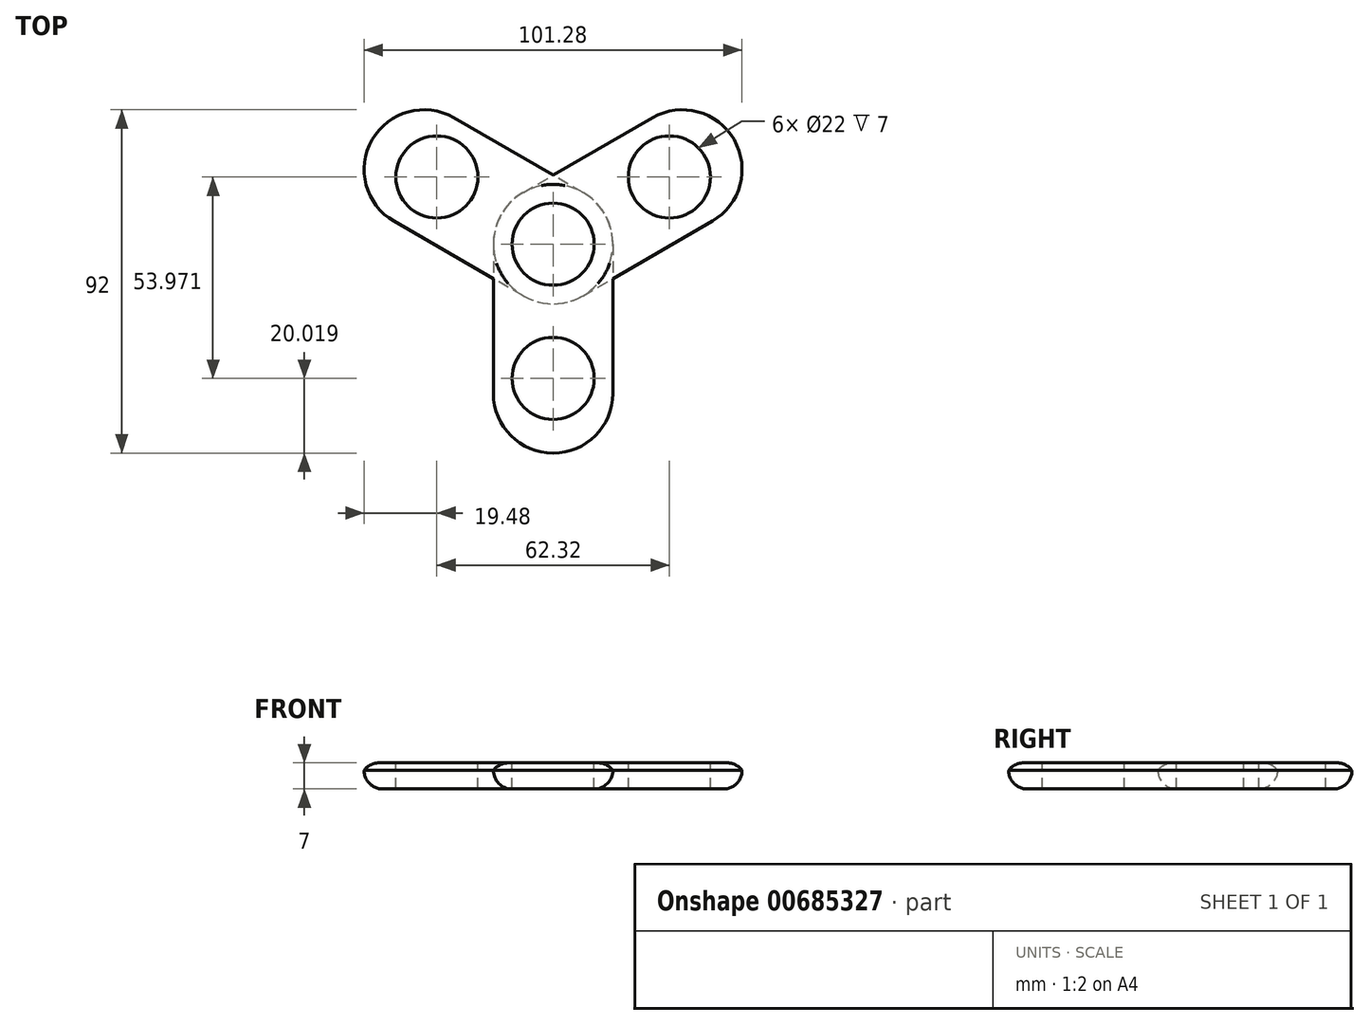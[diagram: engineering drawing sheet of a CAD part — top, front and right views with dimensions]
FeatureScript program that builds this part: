
annotation { "Feature Type Name" : "Feature", "Feature Type Description" : "" }
export const myFeature = defineFeature(function(context is Context, id is Id, definition is map)
    precondition{}
    {
        {
            var Q0;
            Q0=qCreatedBy(makeId("Top.planeOp"),FACE);
            var sketch = newSketch(context, id + "F0", { "sketchPlane" : qUnion([Q0])});
            skCircle(sketch, "E0", {"center": v(0, 0) * mm, "radius": 16 * mm});
            skCircle(sketch, "E1", {"center": v(0, -40) * mm, "radius": 16 * mm});
            skLineSegment(sketch, "E2", {"start": v(16, 0) * mm, "end": v(16, -40) * mm});
            skLineSegment(sketch, "E3", {"start": v(-16, 0) * mm, "end": v(-16, -40) * mm});
            skSolve(sketch);
        }
        {
            var Q0;
            Q0=qSketchRegion(id+"F0",true);
            extrude(context, id + "F1", {"entities" : qUnion([Q0]), "depth" : 7 * mm, "offsetDistance" : 25 * mm});
        }
        {
            var Q0;
            Q0=makeQuery(id+"F1.opExtrude","CAP_FACE",FACE,{"disambiguationData":[OSD([sQuery(id+"F0.wireOp",EDGE,"E0"),sQuery(id+"F0.wireOp",EDGE,"E1"),sQuery(id+"F0.wireOp",EDGE,"E2"),sQuery(id+"F0.wireOp",EDGE,"E3")])],"isStart":false});
            var sketch = newSketch(context, id + "F2", { "sketchPlane" : qUnion([Q0])});
            skCircle(sketch, "E4", {"center": v(0, 0) * mm, "radius": 11 * mm});
            skCircle(sketch, "E5", {"center": v(0, -35.98) * mm, "radius": 11 * mm});
            skSolve(sketch);
        }
        {
            var Q0;
            Q0=qSketchRegion(id+"F2",true);
            extrude(context, id + "F3", {"entities" : qUnion([Q0]), "operationType" : NewBodyOperationType.REMOVE, "oppositeDirection" : true, "depth" : 7 * mm, "offsetDistance" : 25 * mm});
        }
        {
            var Q0;
            Q0=qCreatedBy(makeId("Front.planeOp"),FACE);
            var sketch = newSketch(context, id + "F4", { "sketchPlane" : qUnion([Q0])});
            skLineSegment(sketch, "E6", {"start": v(0, 0) * mm, "end": v(0, 55.38) * mm});
            skSolve(sketch);
        }
        {
            var Q0;
            Q0=makeQuery(id+"F1.opExtrude","SWEPT_BODY",BODY,{"disambiguationData":[OSD([sQuery(id+"F0.wireOp",EDGE,"E0"),sQuery(id+"F0.wireOp",EDGE,"E1"),sQuery(id+"F0.wireOp",EDGE,"E2"),sQuery(id+"F0.wireOp",EDGE,"E3")])]});
            var Q1;
            Q1=sQuery(id+"F4.wireOp",EDGE,"E6");
            circularPattern(context, id + "F5", {"entities" : qUnion([Q0]), "axis" : qUnion([Q1]), "angle" : 360 * degree, "instanceCount" : 3, "equalSpace" : true});
        }
        {
            var Q0;
            Q0=makeQuery(id+"F5.opPattern","COPY",EDGE,{"derivedFrom":makeQuery(id+"F1.opExtrude","CAP_EDGE",EDGE,{"disambiguationData":[OSD([sQuery(id+"F0.wireOp",EDGE,"E3")])],"isStart":true}),"instanceName":"2"});
            var Q1;
            Q1=makeQuery(id+"F5.opPattern","COPY",EDGE,{"derivedFrom":makeQuery(id+"F1.opExtrude","CAP_EDGE",EDGE,{"disambiguationData":[OSD([sQuery(id+"F0.wireOp",EDGE,"E2")])],"isStart":true}),"instanceName":"1"});
            var Q2;
            Q2=makeQuery(id+"F1.opExtrude","CAP_EDGE",EDGE,{"disambiguationData":[OSD([sQuery(id+"F0.wireOp",EDGE,"E2")])],"isStart":true});
            fillet(context, id + "F6", {"entities" : qUnion([Q0, Q1, Q2]), "radius" : 5 * mm, "tangentPropagation" : true, "allowEdgeOverflow" : false});
        }
        {
            var Q0;
            Q0=makeQuery(id+"F5.opPattern","COPY",EDGE,{"derivedFrom":makeQuery(id+"F1.opExtrude","CAP_EDGE",EDGE,{"disambiguationData":[OSD([sQuery(id+"F0.wireOp",EDGE,"E3")])],"isStart":false}),"instanceName":"1"});
            var Q1;
            Q1=makeQuery(id+"F1.opExtrude","CAP_EDGE",EDGE,{"disambiguationData":[OSD([sQuery(id+"F0.wireOp",EDGE,"E2")])],"isStart":false});
            var Q2;
            Q2=makeQuery(id+"F5.opPattern","COPY",EDGE,{"derivedFrom":makeQuery(id+"F1.opExtrude","CAP_EDGE",EDGE,{"disambiguationData":[OSD([sQuery(id+"F0.wireOp",EDGE,"E2")])],"isStart":false}),"instanceName":"2"});
            fillet(context, id + "F7", {"entities" : qUnion([Q0, Q1, Q2]), "radius" : 5 * mm, "tangentPropagation" : true, "allowEdgeOverflow" : false});
        }
    });
